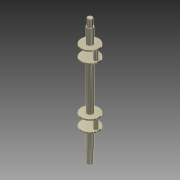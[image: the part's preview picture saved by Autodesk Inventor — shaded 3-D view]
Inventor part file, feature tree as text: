
AUTODESK INVENTOR PART (.ipt)
format: ipt  version: 2015 (Build 190159000, 159)  size: 138,752 bytes
history: native  units: mm
features: extrude x12, sketch x12, chamfer x1
ambient origin geometry x8: Origin, YZ Plane, XZ Plane, XY Plane, X Axis, Y Axis, Z Axis, Center Point
bodies: 实体1 (feature_tree)
feature tree (25):
  extrude  "拉伸1"  Depth=103.0mm TaperAngle=0.0deg
  extrude  "拉伸2"  Depth=5.0mm TaperAngle=0.0deg
  extrude  "拉伸3"  Depth=4.085013mm
  extrude  "拉伸4"  Depth=40.0mm TaperAngle=0.0deg
  extrude  "拉伸5"  Depth=5.0mm TaperAngle=0.0deg
  extrude  "拉伸6"  Depth=190.0mm TaperAngle=0.0deg
  extrude  "拉伸7"  Depth=5.0mm TaperAngle=0.0deg
  extrude  "拉伸8"  Depth=40.0mm TaperAngle=0.0deg
  extrude  "拉伸9"  Depth=5.0mm TaperAngle=0.0deg
  extrude  "拉伸10"  Depth=90.0mm TaperAngle=0.0deg
  chamfer  "倒角2"  Distance=30.0mm
  extrude  "拉伸11"  Depth=22.0mm TaperAngle=45.0deg
  extrude  "拉伸12"  Depth=22.0mm
  sketch  "草图1"  dims[d0=25.0mm d1=103.0mm d2=0.0mm]
  sketch  "草图2"  dims[d3=70.0mm d4=5.0mm d5=0.0mm]
  sketch  "草图3"  dims[d6=15.0mm d7=4.085013mm]
  sketch  "草图4"  dims[d8=24.0mm d9=40.0mm d10=0.0mm]
  sketch  "草图5"  dims[d11=70.0mm d12=5.0mm d13=0.0mm]
  sketch  "草图6"  dims[d14=25.0mm d15=190.0mm d16=0.0mm]
  sketch  "草图7"  dims[d17=70.0mm d18=5.0mm d19=0.0mm]
  sketch  "草图8"  dims[d20=15.0mm d21=40.0mm d22=0.0mm]
  sketch  "草图9"  dims[d23=70.0mm d24=5.0mm d25=0.0mm]
  sketch  "草图10"  dims[d26=25.0mm d27=90.0mm d28=0.0mm]
  sketch  "草图11"  dims[d32=20.0mm]
  sketch  "草图12"  dims[d33=25.0mm d34=30.0mm d35=0.0mm d36=1.0mm d37=2.0mm d38=45.0deg d39=20.0mm d40=25.0mm d41=30.0mm d42=0.0mm d43=20.0mm d44=22.0mm d45=0.0mm]
